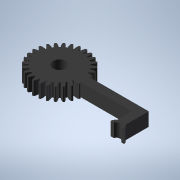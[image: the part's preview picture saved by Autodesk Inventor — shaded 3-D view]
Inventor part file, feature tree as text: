
AUTODESK INVENTOR PART (.ipt)
format: ipt  version: 2022 (Build 260153000, 153)  size: 293,376 bytes
history: native  units: in
note: dims shown in document units (in); Inventor stores cm internally (conversion verified against a paired STEP export)
features: extrude x4, sketch x4, pattern_circular x1
ambient origin geometry x8: Origin, YZ Plane, XZ Plane, XY Plane, X Axis, Y Axis, Z Axis, Center Point
bodies: Solid1 (feature_tree)
feature tree (9):
  extrude  "Extrusion1"  Depth=0.1575in
  pattern_circular  "Circular Pattern1"  [2 undecoded]
  extrude  "Extrusion6"  Depth=0.1772in
  extrude  "Extrusion7"  Depth=0.1969in
  extrude  "Extrusion8"  Depth=0.1969in TaperAngle=0.0deg
  sketch  "Sketch1"  dims[d0=0.6299in d1=0.1575in]
  sketch  "Sketch8"  dims[d2=0.0098in]
  sketch  "Sketch9"  dims[d3=0.0098in]
  sketch  "Sketch10"  dims[d4=0.0236in d7=0.0472in d8=0.1772in d10=0.0787in d11=0.1969in d12=0.0in d13=11.0236in d14=360.0deg d49=0.1969in d50=0.1575in d51=0.5438in d52=0.0in d53=1.1811in d54=0.7087in d55=0.748in d56=0.748in d57=0.1969in d58=0.9843in d59=0.0591in d60=0.0591in d61=0.0591in d62=0.3543in d63=0.0591in d64=0.1181in d65=0.1969in d66=0.0197in d67=0.0197in d68=0.0197in d69=0.1969in d70=0.0in d71=1.1811in d72=0.3543in d73=0.1181in d74=0.1181in d75=0.3543in d76=0.1181in d77=0.1969in d78=0.0197in d79=0.1969in d80=0.0197in d81=0.0197in d82=0.1969in d83=0.0in]
note: 2 required parameter values undecoded (feature->parameter linkage not recoverable at this tier; creation-order binding heuristic only, values carry confidence <= 0.55)
